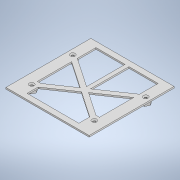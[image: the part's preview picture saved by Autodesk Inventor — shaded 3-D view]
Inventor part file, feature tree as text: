
AUTODESK INVENTOR PART (.ipt)
format: ipt  version: 2020.2 (Build 242310000, 310)  size: 269,824 bytes
history: native  units: mm
features: sketch x4, projected_geometry x4, extrude x3, hole x1
ambient origin geometry x8: Origin, YZ Plane, XZ Plane, XY Plane, X Axis, Y Axis, Z Axis, Center Point
bodies: Solid1 (feature_tree)
feature tree (12):
  extrude  "Extrusion1"  Depth=2.0mm
  extrude  "Extrusion2"  Depth=2.0mm
  hole  "Hole1"  [1 undecoded]
  extrude  "Extrusion3"  Depth=5.0mm
  sketch  "Sketch1"  dims[d0=160.0mm d1=2.0mm]
  sketch  "Sketch2"  dims[d2=2.0mm d3=0.0mm d4=5.5mm]
  sketch  "Sketch3"  dims[d5=5.5mm d6=5.5mm]
  projected_geometry  "Projected Loop1"
  projected_geometry  "Projected Loop2"
  projected_geometry  "Projected Loop3"
  projected_geometry  "Projected Loop4"
  sketch  "Sketch4"  dims[d7=5.5mm d8=81.28mm d9=94.742mm d10=24.999mm d11=35.001mm d12=0.1mm d13=0.1mm d14=0.1mm d15=0.1mm d16=2.0mm d17=2.0mm d18=2.0mm d19=2.0mm d20=5.0mm d21=0.0mm d22=3.4mm d23=6.0mm d24=6.3mm d25=2.0mm d26=90.0deg d27=8.0mm d28=20.594885mm d35=7.0mm d36=7.0mm d37=7.0mm d38=7.0mm d39=7.0mm d40=7.0mm d41=7.0mm d42=7.0mm d43=3.0mm d44=3.0mm d45=3.0mm d46=3.0mm d47=5.0mm d48=0.0mm d49=0.0mm]
note: 1 required parameter value undecoded (feature->parameter linkage not recoverable at this tier; creation-order binding heuristic only, values carry confidence <= 0.55)
